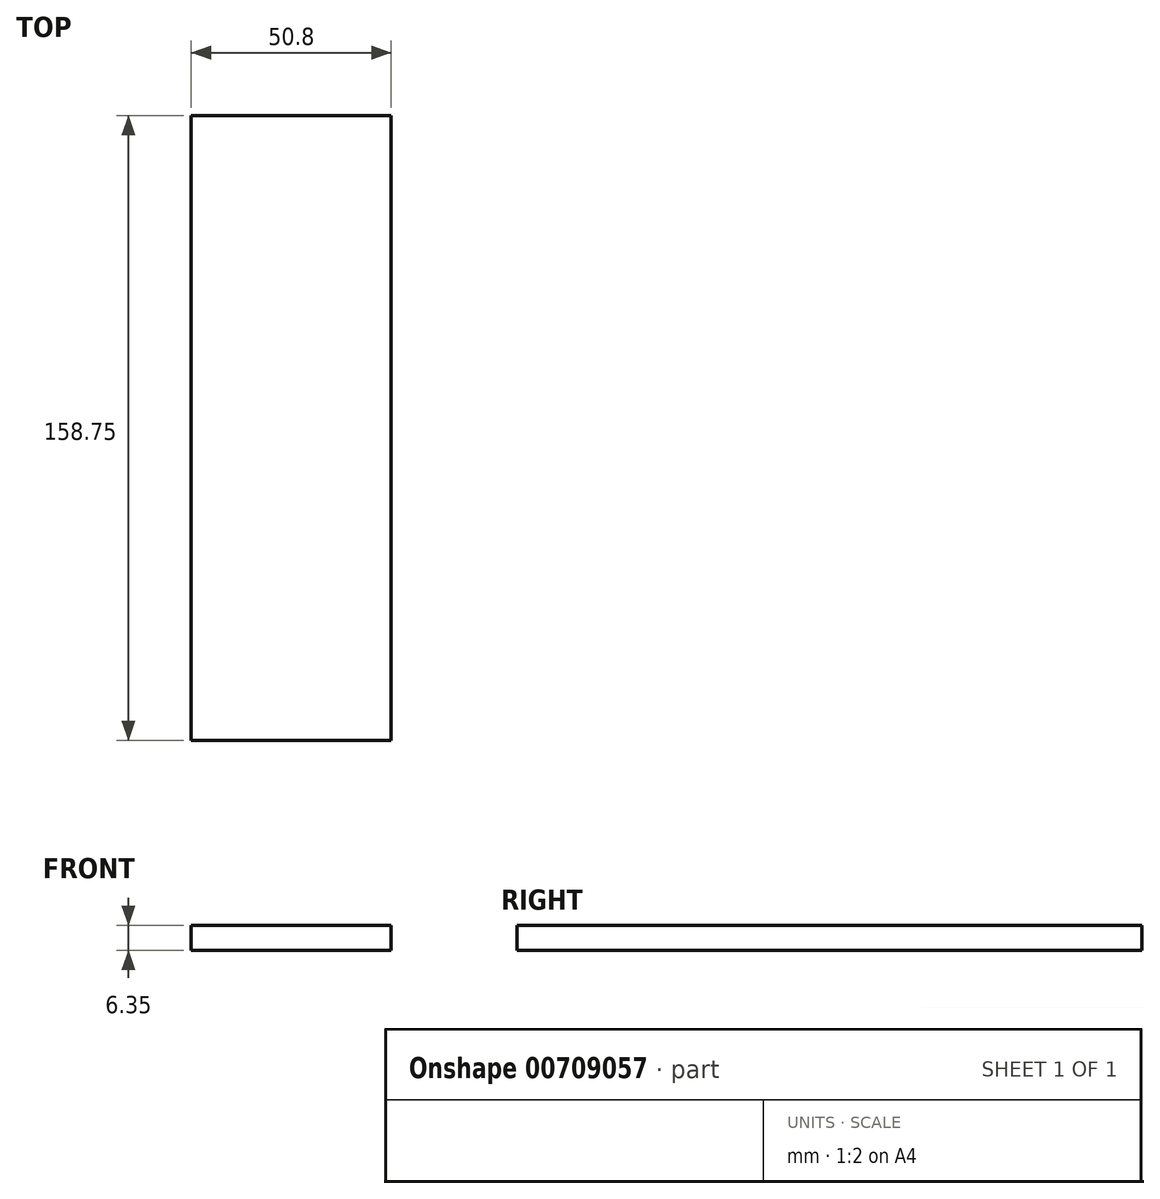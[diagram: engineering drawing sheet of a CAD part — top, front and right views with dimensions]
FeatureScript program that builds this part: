
annotation { "Feature Type Name" : "Feature", "Feature Type Description" : "" }
export const myFeature = defineFeature(function(context is Context, id is Id, definition is map)
    precondition{}
    {
        {
            var Q0;
            Q0=qCreatedBy(makeId("Top.planeOp"),FACE);
            var sketch = newSketch(context, id + "F0", { "sketchPlane" : qUnion([Q0])});
            skLineSegment(sketch, "E0.bottom", {"start": v(0, 0) * mm, "end": v(50.8, 0) * mm});
            skLineSegment(sketch, "E0.top", {"start": v(0, -158.75) * mm, "end": v(50.8, -158.75) * mm});
            skLineSegment(sketch, "E0.left", {"start": v(0, 0) * mm, "end": v(0, -158.75) * mm});
            skLineSegment(sketch, "E0.right", {"start": v(50.8, 0) * mm, "end": v(50.8, -158.75) * mm});
            skSolve(sketch);
        }
        {
            var Q0;
            Q0=makeQuery(id+"F0.imprint","IMPRINT",FACE,{"disambiguationData":[TD([[makeQuery(id+"F0.imprint","IMPRINT",EDGE,{"derivedFrom":sQuery(id+"F0.wireOp",EDGE,"E0.bottom")}),-1.0]])]});
            extrude(context, id + "F1", {"entities" : qUnion([Q0]), "depth" : 6.35 * mm, "offsetDistance" : 25.4 * mm});
        }
    });
